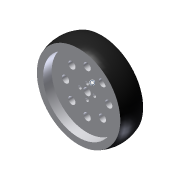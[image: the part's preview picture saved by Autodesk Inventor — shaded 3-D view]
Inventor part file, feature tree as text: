
AUTODESK INVENTOR PART (.ipt)
format: ipt  version: 2013 (Build 170138000, 138)  size: 145,408 bytes
history: native  units: in
note: dims shown in document units (in); Inventor stores cm internally (conversion verified against a paired STEP export)
features: other x4, plane x1
ambient origin geometry x8: Origin, YZ Plane, XZ Plane, XY Plane, X Axis, Y Axis, Z Axis, Center Point
bodies: Solid1 (feature_tree)
feature tree (5):
  other  "Tetrix wheel 4 in.ipt"
  other  "WHEEL_101MM_4-IN_2011::Tetrix wheel 4 in.ipt"
  other  "TaggingFeature1"
  plane  "Work Plane1"
  other  "iComposite:1"
